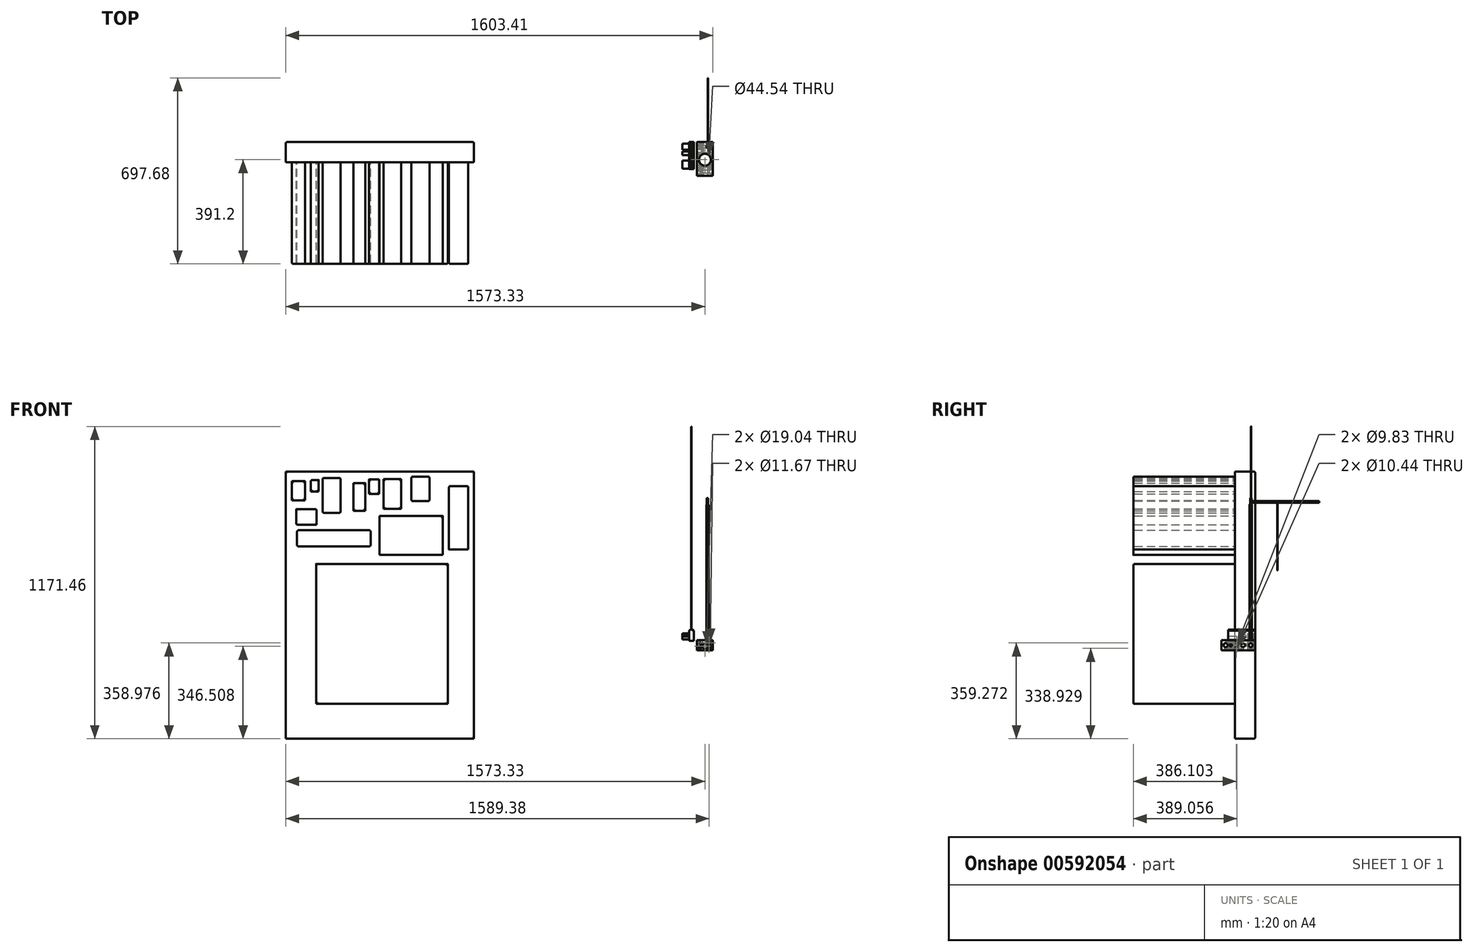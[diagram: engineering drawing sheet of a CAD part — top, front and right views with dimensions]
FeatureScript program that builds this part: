
annotation { "Feature Type Name" : "Feature", "Feature Type Description" : "" }
export const myFeature = defineFeature(function(context is Context, id is Id, definition is map)
    precondition{}
    {
        {
            var Q0;
            Q0=qCreatedBy(makeId("Front.planeOp"),FACE);
            var sketch = newSketch(context, id + "F0", { "sketchPlane" : qUnion([Q0])});
            skLineSegment(sketch, "E0.bottom", {"start": v(30.08, 19.43) * mm, "end": v(-30.08, 19.43) * mm});
            skLineSegment(sketch, "E0.top", {"start": v(30.08, -19.43) * mm, "end": v(-30.08, -19.43) * mm});
            skLineSegment(sketch, "E0.left", {"start": v(30.08, 19.43) * mm, "end": v(30.08, -19.43) * mm});
            skLineSegment(sketch, "E0.right", {"start": v(-30.08, 19.43) * mm, "end": v(-30.08, -19.43) * mm});
            skPoint(sketch, "E0.middle", {"position": v(0, 0) * mm});
            skSolve(sketch);
        }
        {
            var Q0;
            Q0 = qSketchRegion(id + "F0", true);
            extrude(context, id + "F1", {"entities" : qUnion([Q0]), "depth" : 127 * mm, "offsetDistance" : 25.4 * mm});
        }
        {
            var Q0;
            Q0=makeQuery(id+"F1.opExtrude","SWEPT_FACE",FACE,{"disambiguationData":[OSD([sQuery(id+"F0.wireOp",EDGE,"E0.bottom")])]});
            var sketch = newSketch(context, id + "F2", { "sketchPlane" : qUnion([Q0])});
            skCircle(sketch, "E1", {"center": v(0, -66) * mm, "radius": 22.27 * mm});
            skSolve(sketch);
        }
        {
            var Q0;
            Q0=makeQuery(id+"F2.imprint","IMPRINT",FACE,{"disambiguationData":[TD([[makeQuery(id+"F2.imprint","IMPRINT",EDGE,{"derivedFrom":sQuery(id+"F2.wireOp",EDGE,"E1")}),1.0]])]});
            extrude(context, id + "F3", {"entities" : qUnion([Q0]), "operationType" : NewBodyOperationType.REMOVE, "oppositeDirection" : true, "depth" : 127 * mm, "offsetDistance" : 25.4 * mm});
        }
        {
            var Q0;
            Q0=qCreatedBy(makeId("Front.planeOp"),FACE);
            var sketch = newSketch(context, id + "F4", { "sketchPlane" : qUnion([Q0])});
            skLineSegment(sketch, "E2", {"start": v(-59.14, 54.54) * mm, "end": v(-59.14, 17.12) * mm});
            skLineSegment(sketch, "E3", {"start": v(-41.3, 54.83) * mm, "end": v(-41.3, 17.12) * mm});
            skLineSegment(sketch, "E4", {"start": v(-59.14, 54.54) * mm, "end": v(-55.4, 58.77) * mm});
            skLineSegment(sketch, "E5", {"start": v(-55.4, 58.77) * mm, "end": v(-48.5, 58.77) * mm});
            skLineSegment(sketch, "E6", {"start": v(-48.5, 58.77) * mm, "end": v(-41.3, 54.83) * mm});
            skLineSegment(sketch, "E7", {"start": v(-59.14, 17.12) * mm, "end": v(-41.3, 17.12) * mm});
            skSolve(sketch);
        }
        {
            var Q0;
            Q0=makeQuery(id+"F4.imprint","IMPRINT",FACE,{"disambiguationData":[TD([[makeQuery(id+"F4.imprint","IMPRINT",EDGE,{"derivedFrom":sQuery(id+"F4.wireOp",EDGE,"E2")}),1.0]])]});
            extrude(context, id + "F5", {"entities" : qUnion([Q0]), "depth" : 101.6 * mm, "offsetDistance" : 25.4 * mm});
        }
        {
            var Q0;
            Q0=makeQuery(id+"F1.opExtrude","SWEPT_FACE",FACE,{"disambiguationData":[OSD([sQuery(id+"F0.wireOp",EDGE,"E0.left")])]});
            var sketch = newSketch(context, id + "F6", { "sketchPlane" : qUnion([Q0])});
            skCircle(sketch, "E8", {"center": v(-68.14, 8.58) * mm, "radius": 4.91 * mm});
            skSolve(sketch);
        }
        {
            var Q0;
            Q0 = qSketchRegion(id + "F6", true);
            extrude(context, id + "F7", {"entities" : qUnion([Q0]), "operationType" : NewBodyOperationType.REMOVE, "oppositeDirection" : true, "depth" : 254 * mm, "offsetDistance" : 25.4 * mm});
        }
        {
            var Q0;
            Q0=makeQuery(id+"F1.opExtrude","SWEPT_FACE",FACE,{"disambiguationData":[OSD([sQuery(id+"F0.wireOp",EDGE,"E0.left")])]});
            var sketch = newSketch(context, id + "F8", { "sketchPlane" : qUnion([Q0])});
            skCircle(sketch, "E9", {"center": v(-16.75, 0) * mm, "radius": 7.15 * mm});
            skCircle(sketch, "E10", {"center": v(-45.17, 0) * mm, "radius": 7.1 * mm});
            skCircle(sketch, "E11", {"center": v(-71.1, -11.76) * mm, "radius": 5.22 * mm});
            skCircle(sketch, "E12", {"center": v(-91.47, 0) * mm, "radius": 4.6 * mm});
            skCircle(sketch, "E13", {"center": v(-110.6, 0) * mm, "radius": 7.6 * mm});
            skSolve(sketch);
        }
        {
            var Q0;
            Q0=makeQuery(id+"F8.imprint","IMPRINT",FACE,{"disambiguationData":[TD([[makeQuery(id+"F8.imprint","IMPRINT",EDGE,{"derivedFrom":sQuery(id+"F8.wireOp",EDGE,"E13")}),1.0]])]});
            var Q1;
            Q1=makeQuery(id+"F8.imprint","IMPRINT",FACE,{"disambiguationData":[TD([[makeQuery(id+"F8.imprint","IMPRINT",EDGE,{"derivedFrom":sQuery(id+"F8.wireOp",EDGE,"E12")}),1.0]])]});
            var Q2;
            Q2=makeQuery(id+"F8.imprint","IMPRINT",FACE,{"disambiguationData":[TD([[makeQuery(id+"F8.imprint","IMPRINT",EDGE,{"derivedFrom":sQuery(id+"F8.wireOp",EDGE,"E11")}),1.0]])]});
            var Q3;
            Q3=makeQuery(id+"F8.imprint","IMPRINT",FACE,{"disambiguationData":[TD([[makeQuery(id+"F8.imprint","IMPRINT",EDGE,{"derivedFrom":sQuery(id+"F8.wireOp",EDGE,"E10")}),1.0]])]});
            var Q4;
            Q4=makeQuery(id+"F8.imprint","IMPRINT",FACE,{"disambiguationData":[TD([[makeQuery(id+"F8.imprint","IMPRINT",EDGE,{"derivedFrom":sQuery(id+"F8.wireOp",EDGE,"E9")}),1.0]])]});
            extrude(context, id + "F9", {"entities" : qUnion([Q0, Q1, Q2, Q3, Q4]), "operationType" : NewBodyOperationType.REMOVE, "oppositeDirection" : true, "depth" : 254 * mm, "offsetDistance" : 25.4 * mm});
        }
        {
            var Q0;
            Q0=makeQuery(id+"F1.opExtrude","CAP_FACE",FACE,{"disambiguationData":[OSD([sQuery(id+"F0.wireOp",EDGE,"E0.bottom"),sQuery(id+"F0.wireOp",EDGE,"E0.top"),sQuery(id+"F0.wireOp",EDGE,"E0.left"),sQuery(id+"F0.wireOp",EDGE,"E0.right")])],"isStart":false});
            var sketch = newSketch(context, id + "F10", { "sketchPlane" : qUnion([Q0])});
            skCircle(sketch, "E14", {"center": v(-17.6, -8.4) * mm, "radius": 4.93 * mm});
            skCircle(sketch, "E15", {"center": v(-17, 7.55) * mm, "radius": 2.32 * mm});
            skCircle(sketch, "E16", {"center": v(-9.56, 5.12) * mm, "radius": 3.65 * mm});
            skCircle(sketch, "E17", {"center": v(0, -4.18) * mm, "radius": 9.52 * mm});
            skCircle(sketch, "E18", {"center": v(16.04, 8.29) * mm, "radius": 5.84 * mm});
            skCircle(sketch, "E19", {"center": v(21.54, -7.8) * mm, "radius": 4.4 * mm});
            skCircle(sketch, "E20", {"center": v(13.11, -13.57) * mm, "radius": 4.08 * mm});
            skSolve(sketch);
        }
        {
            var Q0;
            Q0 = qSketchRegion(id + "F10", true);
            extrude(context, id + "F11", {"entities" : qUnion([Q0]), "operationType" : NewBodyOperationType.REMOVE, "oppositeDirection" : true, "depth" : 254 * mm, "offsetDistance" : 25.4 * mm});
        }
        {
            var Q0;
            Q0=makeQuery(id+"F5.opExtrude","SWEPT_FACE",FACE,{"disambiguationData":[OSD([sQuery(id+"F4.wireOp",EDGE,"E2")])]});
            var sketch = newSketch(context, id + "F12", { "sketchPlane" : qUnion([Q0])});
            skLineSegment(sketch, "E21.bottom", {"start": v(69.72, 33) * mm, "end": v(99.84, 33) * mm});
            skLineSegment(sketch, "E21.top", {"start": v(69.72, 21.6) * mm, "end": v(99.84, 21.6) * mm});
            skLineSegment(sketch, "E21.left", {"start": v(69.72, 33) * mm, "end": v(69.72, 21.6) * mm});
            skLineSegment(sketch, "E21.right", {"start": v(99.84, 33) * mm, "end": v(99.84, 21.6) * mm});
            skPoint(sketch, "E21.middle", {"position": v(84.78, 27.3) * mm});
            skLineSegment(sketch, "E22.bottom", {"start": v(34.78, 37.75) * mm, "end": v(48.36, 37.75) * mm});
            skLineSegment(sketch, "E22.top", {"start": v(34.78, 31.82) * mm, "end": v(48.36, 31.82) * mm});
            skLineSegment(sketch, "E22.left", {"start": v(34.78, 37.75) * mm, "end": v(34.78, 31.82) * mm});
            skLineSegment(sketch, "E22.right", {"start": v(48.36, 37.75) * mm, "end": v(48.36, 31.82) * mm});
            skPoint(sketch, "E22.middle", {"position": v(41.57, 34.78) * mm});
            skLineSegment(sketch, "E23.bottom", {"start": v(28.18, 25.53) * mm, "end": v(5.18, 25.53) * mm});
            skLineSegment(sketch, "E23.top", {"start": v(28.18, 44.88) * mm, "end": v(5.18, 44.88) * mm});
            skLineSegment(sketch, "E23.left", {"start": v(28.18, 25.53) * mm, "end": v(28.18, 44.88) * mm});
            skLineSegment(sketch, "E23.right", {"start": v(5.18, 25.53) * mm, "end": v(5.18, 44.88) * mm});
            skPoint(sketch, "E23.middle", {"position": v(16.68, 35.2) * mm});
            skSolve(sketch);
        }
        {
            var Q0;
            Q0 = qSketchRegion(id + "F12", true);
            extrude(context, id + "F13", {"entities" : qUnion([Q0]), "operationType" : NewBodyOperationType.ADD, "depth" : 25.4 * mm, "offsetDistance" : 25.4 * mm});
        }
        {
            var Q0;
            Q0=makeQuery(id+"F1.opExtrude","SWEPT_FACE",FACE,{"disambiguationData":[OSD([sQuery(id+"F0.wireOp",EDGE,"E0.bottom")])]});
            var sketch = newSketch(context, id + "F14", { "sketchPlane" : qUnion([Q0])});
            skCircle(sketch, "E24", {"center": v(9.27, -17.23) * mm, "radius": 4.37 * mm});
            skSolve(sketch);
        }
        {
            var Q0;
            Q0 = qSketchRegion(id + "F14", true);
            extrude(context, id + "F15", {"entities" : qUnion([Q0]), "operationType" : NewBodyOperationType.ADD, "depth" : 508 * mm, "offsetDistance" : 25.4 * mm});
        }
        {
            var Q0;
            Q0=makeQuery(id+"F5.opExtrude","SWEPT_FACE",FACE,{"disambiguationData":[OSD([sQuery(id+"F4.wireOp",EDGE,"E5")])]});
            var sketch = newSketch(context, id + "F16", { "sketchPlane" : qUnion([Q0])});
            skCircle(sketch, "E25", {"center": v(-51.42, -15.39) * mm, "radius": 0.57 * mm});
            skSolve(sketch);
        }
        {
            var Q0;
            Q0 = qSketchRegion(id + "F16", true);
            extrude(context, id + "F17", {"entities" : qUnion([Q0]), "operationType" : NewBodyOperationType.ADD, "depth" : 762 * mm, "offsetDistance" : 25.4 * mm});
        }
        {
            var Q0;
            Q0=makeQuery(id+"F15.opExtrude","CAP_FACE",FACE,{"disambiguationData":[OSD([sQuery(id+"F14.wireOp",EDGE,"E24")])],"isStart":false});
            var sketch = newSketch(context, id + "F18", { "sketchPlane" : qUnion([Q0])});
            skLineSegment(sketch, "E26.bottom", {"start": v(9.3, -16.3) * mm, "end": v(11.43, -16.3) * mm});
            skLineSegment(sketch, "E26.top", {"start": v(9.3, -13.52) * mm, "end": v(11.43, -13.52) * mm});
            skLineSegment(sketch, "E26.left", {"start": v(9.3, -16.3) * mm, "end": v(9.3, -13.52) * mm});
            skLineSegment(sketch, "E26.right", {"start": v(11.43, -16.3) * mm, "end": v(11.43, -13.52) * mm});
            skPoint(sketch, "E26.middle", {"position": v(10.37, -14.9) * mm});
            skLineSegment(sketch, "E27.bottom", {"start": v(8.92, -18.51) * mm, "end": v(9.91, -18.51) * mm});
            skLineSegment(sketch, "E27.top", {"start": v(8.92, -16.37) * mm, "end": v(9.91, -16.37) * mm});
            skLineSegment(sketch, "E27.left", {"start": v(8.92, -18.51) * mm, "end": v(8.92, -16.37) * mm});
            skLineSegment(sketch, "E27.right", {"start": v(9.91, -18.51) * mm, "end": v(9.91, -16.37) * mm});
            skPoint(sketch, "E27.middle", {"position": v(9.42, -17.44) * mm});
            skLineSegment(sketch, "E28.bottom", {"start": v(6.4, -17.92) * mm, "end": v(8.35, -17.92) * mm});
            skLineSegment(sketch, "E28.top", {"start": v(6.4, -14.7) * mm, "end": v(8.35, -14.7) * mm});
            skLineSegment(sketch, "E28.left", {"start": v(6.4, -17.92) * mm, "end": v(6.4, -14.7) * mm});
            skLineSegment(sketch, "E28.right", {"start": v(8.35, -17.92) * mm, "end": v(8.35, -14.7) * mm});
            skPoint(sketch, "E28.middle", {"position": v(7.37, -16.31) * mm});
            skSolve(sketch);
        }
        {
            var Q0;
            Q0 = qSketchRegion(id + "F18", true);
            extrude(context, id + "F19", {"entities" : qUnion([Q0]), "operationType" : NewBodyOperationType.ADD, "depth" : 25.4 * mm, "offsetDistance" : 25.4 * mm});
        }
        {
            var Q0;
            Q0=makeQuery(id+"F19.opExtrude","SWEPT_FACE",FACE,{"disambiguationData":[OSD([sQuery(id+"F18.wireOp",EDGE,"E26.top")])]});
            var sketch = newSketch(context, id + "F20", { "sketchPlane" : qUnion([Q0])});
            skLineSegment(sketch, "E29.bottom", {"start": v(-10, 540.96) * mm, "end": v(-11.1, 540.96) * mm});
            skLineSegment(sketch, "E29.top", {"start": v(-10, 534.92) * mm, "end": v(-11.1, 534.92) * mm});
            skLineSegment(sketch, "E29.left", {"start": v(-10, 540.96) * mm, "end": v(-10, 534.92) * mm});
            skLineSegment(sketch, "E29.right", {"start": v(-11.1, 540.96) * mm, "end": v(-11.1, 534.92) * mm});
            skPoint(sketch, "E29.middle", {"position": v(-10.55, 537.94) * mm});
            skSolve(sketch);
        }
        {
            var Q0;
            Q0 = qSketchRegion(id + "F20", true);
            extrude(context, id + "F21", {"entities" : qUnion([Q0]), "operationType" : NewBodyOperationType.ADD, "depth" : 254 * mm, "offsetDistance" : 25.4 * mm});
        }
        {
            var Q0;
            Q0=makeQuery(id+"F21.opExtrude","SWEPT_FACE",FACE,{"disambiguationData":[OSD([sQuery(id+"F20.wireOp",EDGE,"E29.top")])]});
            var sketch = newSketch(context, id + "F22", { "sketchPlane" : qUnion([Q0])});
            skCircle(sketch, "E30", {"center": v(10.57, -83.53) * mm, "radius": 0.18 * mm});
            skSolve(sketch);
        }
        {
            var Q0;
            Q0 = qSketchRegion(id + "F22", true);
            extrude(context, id + "F23", {"entities" : qUnion([Q0]), "operationType" : NewBodyOperationType.ADD, "depth" : 254 * mm, "offsetDistance" : 25.4 * mm});
        }
        {
            var Q0;
            Q0=qCreatedBy(makeId("Front.planeOp"),FACE);
            var sketch = newSketch(context, id + "F24", { "sketchPlane" : qUnion([Q0])});
            skLineSegment(sketch, "E31.bottom", {"start": v(-866.82, -350.69) * mm, "end": v(-1573.33, -350.69) * mm});
            skLineSegment(sketch, "E31.top", {"start": v(-866.82, 652.1) * mm, "end": v(-1573.33, 652.1) * mm});
            skLineSegment(sketch, "E31.left", {"start": v(-866.82, -350.69) * mm, "end": v(-866.82, 652.1) * mm});
            skLineSegment(sketch, "E31.right", {"start": v(-1573.33, -350.69) * mm, "end": v(-1573.33, 652.1) * mm});
            skPoint(sketch, "E31.middle", {"position": v(-1220.07, 150.7) * mm});
            skSolve(sketch);
        }
        {
            var Q0;
            Q0 = qSketchRegion(id + "F24", true);
            extrude(context, id + "F25", {"entities" : qUnion([Q0]), "depth" : 76.2 * mm, "offsetDistance" : 25.4 * mm});
        }
        {
            var Q0;
            Q0=makeQuery(id+"F25.opExtrude","CAP_FACE",FACE,{"disambiguationData":[OSD([sQuery(id+"F24.wireOp",EDGE,"E31.bottom"),sQuery(id+"F24.wireOp",EDGE,"E31.top"),sQuery(id+"F24.wireOp",EDGE,"E31.left"),sQuery(id+"F24.wireOp",EDGE,"E31.right")])],"isStart":false});
            var sketch = newSketch(context, id + "F26", { "sketchPlane" : qUnion([Q0])});
            skLineSegment(sketch, "E32.bottom", {"start": v(-1501.2, 544.2) * mm, "end": v(-1550.28, 544.2) * mm});
            skLineSegment(sketch, "E32.top", {"start": v(-1501.2, 615.35) * mm, "end": v(-1550.28, 615.35) * mm});
            skLineSegment(sketch, "E32.left", {"start": v(-1501.2, 544.2) * mm, "end": v(-1501.2, 615.35) * mm});
            skLineSegment(sketch, "E32.right", {"start": v(-1550.28, 544.2) * mm, "end": v(-1550.28, 615.35) * mm});
            skPoint(sketch, "E32.middle", {"position": v(-1525.74, 579.77) * mm});
            skLineSegment(sketch, "E33.bottom", {"start": v(-1449.84, 576.02) * mm, "end": v(-1479.44, 576.02) * mm});
            skLineSegment(sketch, "E33.top", {"start": v(-1449.84, 619.96) * mm, "end": v(-1479.44, 619.96) * mm});
            skLineSegment(sketch, "E33.left", {"start": v(-1449.84, 576.02) * mm, "end": v(-1449.84, 619.96) * mm});
            skLineSegment(sketch, "E33.right", {"start": v(-1479.44, 576.02) * mm, "end": v(-1479.44, 619.96) * mm});
            skPoint(sketch, "E33.middle", {"position": v(-1464.64, 598) * mm});
            skLineSegment(sketch, "E34.bottom", {"start": v(-1457.86, 452.43) * mm, "end": v(-1533.97, 452.43) * mm});
            skLineSegment(sketch, "E34.top", {"start": v(-1457.86, 510.53) * mm, "end": v(-1533.97, 510.53) * mm});
            skLineSegment(sketch, "E34.left", {"start": v(-1457.86, 452.43) * mm, "end": v(-1457.86, 510.53) * mm});
            skLineSegment(sketch, "E34.right", {"start": v(-1533.97, 452.43) * mm, "end": v(-1533.97, 510.53) * mm});
            skPoint(sketch, "E34.middle", {"position": v(-1495.92, 481.48) * mm});
            skLineSegment(sketch, "E35.bottom", {"start": v(-1367.21, 497.11) * mm, "end": v(-1435.46, 497.11) * mm});
            skLineSegment(sketch, "E35.top", {"start": v(-1367.21, 627.57) * mm, "end": v(-1435.46, 627.57) * mm});
            skLineSegment(sketch, "E35.left", {"start": v(-1367.21, 497.11) * mm, "end": v(-1367.21, 627.57) * mm});
            skLineSegment(sketch, "E35.right", {"start": v(-1435.46, 497.11) * mm, "end": v(-1435.46, 627.57) * mm});
            skPoint(sketch, "E35.middle", {"position": v(-1401.34, 562.34) * mm});
            skLineSegment(sketch, "E36.bottom", {"start": v(-1274.2, 503.97) * mm, "end": v(-1318.99, 503.97) * mm});
            skLineSegment(sketch, "E36.top", {"start": v(-1274.2, 608.19) * mm, "end": v(-1318.99, 608.19) * mm});
            skLineSegment(sketch, "E36.left", {"start": v(-1274.2, 503.97) * mm, "end": v(-1274.2, 608.19) * mm});
            skLineSegment(sketch, "E36.right", {"start": v(-1318.99, 503.97) * mm, "end": v(-1318.99, 608.19) * mm});
            skPoint(sketch, "E36.middle", {"position": v(-1296.6, 556.08) * mm});
            skLineSegment(sketch, "E37.bottom", {"start": v(-1254.63, 371.16) * mm, "end": v(-1530.85, 371.16) * mm});
            skLineSegment(sketch, "E37.top", {"start": v(-1254.63, 431.29) * mm, "end": v(-1530.85, 431.29) * mm});
            skLineSegment(sketch, "E37.left", {"start": v(-1254.63, 371.16) * mm, "end": v(-1254.63, 431.29) * mm});
            skLineSegment(sketch, "E37.right", {"start": v(-1530.85, 371.16) * mm, "end": v(-1530.85, 431.29) * mm});
            skPoint(sketch, "E37.middle", {"position": v(-1392.74, 401.22) * mm});
            skLineSegment(sketch, "E38.bottom", {"start": v(-1222.51, 567.89) * mm, "end": v(-1261.5, 567.89) * mm});
            skLineSegment(sketch, "E38.top", {"start": v(-1222.51, 622.32) * mm, "end": v(-1261.5, 622.32) * mm});
            skLineSegment(sketch, "E38.left", {"start": v(-1222.51, 567.89) * mm, "end": v(-1222.51, 622.32) * mm});
            skLineSegment(sketch, "E38.right", {"start": v(-1261.5, 567.89) * mm, "end": v(-1261.5, 622.32) * mm});
            skPoint(sketch, "E38.middle", {"position": v(-1242, 595.1) * mm});
            skLineSegment(sketch, "E39.bottom", {"start": v(-965.38, -220.28) * mm, "end": v(-1459, -220.28) * mm});
            skLineSegment(sketch, "E39.top", {"start": v(-965.38, 304.92) * mm, "end": v(-1459, 304.92) * mm});
            skLineSegment(sketch, "E39.left", {"start": v(-965.38, -220.28) * mm, "end": v(-965.38, 304.92) * mm});
            skLineSegment(sketch, "E39.right", {"start": v(-1459, -220.28) * mm, "end": v(-1459, 304.92) * mm});
            skPoint(sketch, "E39.middle", {"position": v(-1212.2, 42.32) * mm});
            skLineSegment(sketch, "E40.bottom", {"start": v(-1140.45, 511.24) * mm, "end": v(-1206.51, 511.24) * mm});
            skLineSegment(sketch, "E40.top", {"start": v(-1140.45, 623.03) * mm, "end": v(-1206.51, 623.03) * mm});
            skLineSegment(sketch, "E40.left", {"start": v(-1140.45, 511.24) * mm, "end": v(-1140.45, 623.03) * mm});
            skLineSegment(sketch, "E40.right", {"start": v(-1206.51, 511.24) * mm, "end": v(-1206.51, 623.03) * mm});
            skPoint(sketch, "E40.middle", {"position": v(-1173.48, 567.14) * mm});
            skLineSegment(sketch, "E41.bottom", {"start": v(-1033.75, 540.67) * mm, "end": v(-1101.6, 540.67) * mm});
            skLineSegment(sketch, "E41.top", {"start": v(-1033.75, 632.82) * mm, "end": v(-1101.6, 632.82) * mm});
            skLineSegment(sketch, "E41.left", {"start": v(-1033.75, 540.67) * mm, "end": v(-1033.75, 632.82) * mm});
            skLineSegment(sketch, "E41.right", {"start": v(-1101.6, 540.67) * mm, "end": v(-1101.6, 632.82) * mm});
            skPoint(sketch, "E41.middle", {"position": v(-1067.67, 586.74) * mm});
            skLineSegment(sketch, "E42.bottom", {"start": v(-983.66, 338.54) * mm, "end": v(-1221, 338.54) * mm});
            skLineSegment(sketch, "E42.top", {"start": v(-983.66, 485.04) * mm, "end": v(-1221, 485.04) * mm});
            skLineSegment(sketch, "E42.left", {"start": v(-983.66, 338.54) * mm, "end": v(-983.66, 485.04) * mm});
            skLineSegment(sketch, "E42.right", {"start": v(-1221, 338.54) * mm, "end": v(-1221, 485.04) * mm});
            skPoint(sketch, "E42.middle", {"position": v(-1102.33, 411.8) * mm});
            skLineSegment(sketch, "E43.bottom", {"start": v(-888.13, 358.82) * mm, "end": v(-960.78, 358.82) * mm});
            skLineSegment(sketch, "E43.top", {"start": v(-888.13, 597.01) * mm, "end": v(-960.78, 597.01) * mm});
            skLineSegment(sketch, "E43.left", {"start": v(-888.13, 358.82) * mm, "end": v(-888.13, 597.01) * mm});
            skLineSegment(sketch, "E43.right", {"start": v(-960.78, 358.82) * mm, "end": v(-960.78, 597.01) * mm});
            skPoint(sketch, "E43.middle", {"position": v(-924.46, 477.92) * mm});
            skSolve(sketch);
        }
        {
            var Q0;
            Q0 = qSketchRegion(id + "F26", true);
            extrude(context, id + "F27", {"entities" : qUnion([Q0]), "operationType" : NewBodyOperationType.ADD, "depth" : 381 * mm, "offsetDistance" : 25.4 * mm});
        }
        {
            var Q0;
            Q0=makeQuery(id+"F27.opExtrude","SWEPT_EDGE",EDGE,{"disambiguationData":[OSD([sQuery(id+"F26.wireOp",EDGE,"E43.top"),sQuery(id+"F26.wireOp",EDGE,"E43.left")])]});
            fillet(context, id + "F28", {"entities" : qUnion([Q0]), "radius" : 5.08 * mm, "tangentPropagation" : true, "allowEdgeOverflow" : false});
        }
        {
            var Q0;
            Q0=makeQuery(id+"F27.opExtrude","SWEPT_EDGE",EDGE,{"disambiguationData":[OSD([sQuery(id+"F26.wireOp",EDGE,"E43.top"),sQuery(id+"F26.wireOp",EDGE,"E43.right")])]});
            var Q1;
            Q1=makeQuery(id+"F27.opExtrude","CAP_EDGE",EDGE,{"disambiguationData":[OSD([sQuery(id+"F26.wireOp",EDGE,"E43.right")])],"isStart":false});
            var Q2;
            Q2=makeQuery(id+"F27.opExtrude","CAP_EDGE",EDGE,{"disambiguationData":[OSD([sQuery(id+"F26.wireOp",EDGE,"E43.right")])],"isStart":true});
            var Q3;
            Q3=makeQuery(id+"F27.opExtrude","CAP_EDGE",EDGE,{"disambiguationData":[OSD([sQuery(id+"F26.wireOp",EDGE,"E42.top")])],"isStart":false});
            var Q4;
            Q4=makeQuery(id+"F27.opExtrude","CAP_EDGE",EDGE,{"disambiguationData":[OSD([sQuery(id+"F26.wireOp",EDGE,"E42.left")])],"isStart":false});
            var Q5;
            Q5=makeQuery(id+"F27.opExtrude","CAP_EDGE",EDGE,{"disambiguationData":[OSD([sQuery(id+"F26.wireOp",EDGE,"E41.bottom")])],"isStart":false});
            var Q6;
            Q6=makeQuery(id+"F27.opExtrude","CAP_EDGE",EDGE,{"disambiguationData":[OSD([sQuery(id+"F26.wireOp",EDGE,"E41.left")])],"isStart":false});
            var Q7;
            Q7=makeQuery(id+"F27.opExtrude","SWEPT_EDGE",EDGE,{"disambiguationData":[OSD([sQuery(id+"F26.wireOp",EDGE,"E41.bottom"),sQuery(id+"F26.wireOp",EDGE,"E41.left")])]});
            fillet(context, id + "F29", {"entities" : qUnion([Q0, Q1, Q2, Q3, Q4, Q5, Q6, Q7]), "radius" : 5.08 * mm, "tangentPropagation" : true, "allowEdgeOverflow" : false});
        }
        {
            var Q0;
            Q0=makeQuery(id+"F27.opExtrude","CAP_EDGE",EDGE,{"disambiguationData":[OSD([sQuery(id+"F26.wireOp",EDGE,"E43.top")])],"isStart":false});
            fillet(context, id + "F30", {"entities" : qUnion([Q0]), "radius" : 5.08 * mm, "tangentPropagation" : true, "allowEdgeOverflow" : false});
        }
        {
            var Q0;
            Q0=makeQuery(id+"F27.opExtrude","CAP_EDGE",EDGE,{"disambiguationData":[OSD([sQuery(id+"F26.wireOp",EDGE,"E41.right")])],"isStart":false});
            var Q1;
            Q1=makeQuery(id+"F27.opExtrude","SWEPT_EDGE",EDGE,{"disambiguationData":[OSD([sQuery(id+"F26.wireOp",EDGE,"E41.top"),sQuery(id+"F26.wireOp",EDGE,"E41.right")])]});
            var Q2;
            Q2=makeQuery(id+"F27.opExtrude","CAP_EDGE",EDGE,{"disambiguationData":[OSD([sQuery(id+"F26.wireOp",EDGE,"E41.top")])],"isStart":false});
            var Q3;
            Q3=makeQuery(id+"F27.opExtrude","SWEPT_EDGE",EDGE,{"disambiguationData":[OSD([sQuery(id+"F26.wireOp",EDGE,"E41.top"),sQuery(id+"F26.wireOp",EDGE,"E41.left")])]});
            fillet(context, id + "F31", {"entities" : qUnion([Q0, Q1, Q2, Q3]), "radius" : 5.08 * mm, "tangentPropagation" : true, "allowEdgeOverflow" : false});
        }
        {
            var Q0;
            Q0=makeQuery(id+"F27.opExtrude","CAP_EDGE",EDGE,{"disambiguationData":[OSD([sQuery(id+"F26.wireOp",EDGE,"E39.top")])],"isStart":false});
            var Q1;
            Q1=makeQuery(id+"F27.opExtrude","CAP_EDGE",EDGE,{"disambiguationData":[OSD([sQuery(id+"F26.wireOp",EDGE,"E39.left")])],"isStart":false});
            var Q2;
            Q2=makeQuery(id+"F27.opExtrude","CAP_EDGE",EDGE,{"disambiguationData":[OSD([sQuery(id+"F26.wireOp",EDGE,"E39.bottom")])],"isStart":false});
            var Q3;
            Q3=makeQuery(id+"F27.opExtrude","CAP_EDGE",EDGE,{"disambiguationData":[OSD([sQuery(id+"F26.wireOp",EDGE,"E39.right")])],"isStart":false});
            var Q4;
            Q4=makeQuery(id+"F27.opExtrude","CAP_EDGE",EDGE,{"disambiguationData":[OSD([sQuery(id+"F26.wireOp",EDGE,"E37.bottom")])],"isStart":false});
            var Q5;
            Q5=makeQuery(id+"F27.opExtrude","CAP_EDGE",EDGE,{"disambiguationData":[OSD([sQuery(id+"F26.wireOp",EDGE,"E37.top")])],"isStart":false});
            var Q6;
            Q6=makeQuery(id+"F27.opExtrude","CAP_EDGE",EDGE,{"disambiguationData":[OSD([sQuery(id+"F26.wireOp",EDGE,"E35.left")])],"isStart":false});
            var Q7;
            Q7=makeQuery(id+"F27.opExtrude","CAP_EDGE",EDGE,{"disambiguationData":[OSD([sQuery(id+"F26.wireOp",EDGE,"E35.right")])],"isStart":false});
            fillet(context, id + "F32", {"entities" : qUnion([Q0, Q1, Q2, Q3, Q4, Q5, Q6, Q7]), "radius" : 5.08 * mm, "tangentPropagation" : true, "allowEdgeOverflow" : false});
        }
        {
            var Q0;
            Q0=makeQuery(id+"F27.opExtrude","CAP_EDGE",EDGE,{"disambiguationData":[OSD([sQuery(id+"F26.wireOp",EDGE,"E37.left")])],"isStart":false});
            var Q1;
            Q1=makeQuery(id+"F27.opExtrude","CAP_EDGE",EDGE,{"disambiguationData":[OSD([sQuery(id+"F26.wireOp",EDGE,"E34.left")])],"isStart":false});
            var Q2;
            Q2=makeQuery(id+"F27.opExtrude","CAP_EDGE",EDGE,{"disambiguationData":[OSD([sQuery(id+"F26.wireOp",EDGE,"E34.bottom")])],"isStart":false});
            fillet(context, id + "F33", {"entities" : qUnion([Q0, Q1, Q2]), "radius" : 5.08 * mm, "tangentPropagation" : true, "allowEdgeOverflow" : false});
        }
        {
            var Q0;
            Q0=makeQuery(id+"F27.opExtrude","CAP_EDGE",EDGE,{"disambiguationData":[OSD([sQuery(id+"F26.wireOp",EDGE,"E37.right")])],"isStart":false});
            var Q1;
            Q1=makeQuery(id+"F27.opExtrude","CAP_EDGE",EDGE,{"disambiguationData":[OSD([sQuery(id+"F26.wireOp",EDGE,"E34.right")])],"isStart":false});
            var Q2;
            Q2=makeQuery(id+"F27.opExtrude","CAP_EDGE",EDGE,{"disambiguationData":[OSD([sQuery(id+"F26.wireOp",EDGE,"E34.top")])],"isStart":false});
            var Q3;
            Q3=makeQuery(id+"F27.opExtrude","CAP_EDGE",EDGE,{"disambiguationData":[OSD([sQuery(id+"F26.wireOp",EDGE,"E32.bottom")])],"isStart":false});
            var Q4;
            Q4=makeQuery(id+"F27.opExtrude","CAP_EDGE",EDGE,{"disambiguationData":[OSD([sQuery(id+"F26.wireOp",EDGE,"E32.left")])],"isStart":false});
            var Q5;
            Q5=makeQuery(id+"F27.opExtrude","CAP_EDGE",EDGE,{"disambiguationData":[OSD([sQuery(id+"F26.wireOp",EDGE,"E32.right")])],"isStart":false});
            var Q6;
            Q6=makeQuery(id+"F27.opExtrude","CAP_EDGE",EDGE,{"disambiguationData":[OSD([sQuery(id+"F26.wireOp",EDGE,"E35.bottom")])],"isStart":false});
            var Q7;
            Q7=makeQuery(id+"F27.opExtrude","CAP_EDGE",EDGE,{"disambiguationData":[OSD([sQuery(id+"F26.wireOp",EDGE,"E33.bottom")])],"isStart":false});
            var Q8;
            Q8=makeQuery(id+"F27.opExtrude","CAP_EDGE",EDGE,{"disambiguationData":[OSD([sQuery(id+"F26.wireOp",EDGE,"E33.left")])],"isStart":false});
            var Q9;
            Q9=makeQuery(id+"F27.opExtrude","CAP_EDGE",EDGE,{"disambiguationData":[OSD([sQuery(id+"F26.wireOp",EDGE,"E33.right")])],"isStart":false});
            var Q10;
            Q10=makeQuery(id+"F27.opExtrude","CAP_EDGE",EDGE,{"disambiguationData":[OSD([sQuery(id+"F26.wireOp",EDGE,"E33.top")])],"isStart":false});
            var Q11;
            Q11=makeQuery(id+"F27.opExtrude","CAP_EDGE",EDGE,{"disambiguationData":[OSD([sQuery(id+"F26.wireOp",EDGE,"E32.top")])],"isStart":false});
            var Q12;
            Q12=makeQuery(id+"F27.opExtrude","CAP_EDGE",EDGE,{"disambiguationData":[OSD([sQuery(id+"F26.wireOp",EDGE,"E35.top")])],"isStart":false});
            var Q13;
            Q13=makeQuery(id+"F27.opExtrude","CAP_EDGE",EDGE,{"disambiguationData":[OSD([sQuery(id+"F26.wireOp",EDGE,"E36.top")])],"isStart":false});
            var Q14;
            Q14=makeQuery(id+"F27.opExtrude","CAP_EDGE",EDGE,{"disambiguationData":[OSD([sQuery(id+"F26.wireOp",EDGE,"E36.right")])],"isStart":false});
            var Q15;
            Q15=makeQuery(id+"F27.opExtrude","CAP_EDGE",EDGE,{"disambiguationData":[OSD([sQuery(id+"F26.wireOp",EDGE,"E36.left")])],"isStart":false});
            var Q16;
            Q16=makeQuery(id+"F27.opExtrude","CAP_EDGE",EDGE,{"disambiguationData":[OSD([sQuery(id+"F26.wireOp",EDGE,"E36.bottom")])],"isStart":false});
            var Q17;
            Q17=makeQuery(id+"F27.opExtrude","CAP_EDGE",EDGE,{"disambiguationData":[OSD([sQuery(id+"F26.wireOp",EDGE,"E38.bottom")])],"isStart":false});
            var Q18;
            Q18=makeQuery(id+"F27.opExtrude","CAP_EDGE",EDGE,{"disambiguationData":[OSD([sQuery(id+"F26.wireOp",EDGE,"E38.left")])],"isStart":false});
            var Q19;
            Q19=makeQuery(id+"F25.opExtrude","CAP_FACE",FACE,{"disambiguationData":[OSD([sQuery(id+"F24.wireOp",EDGE,"E31.bottom"),sQuery(id+"F24.wireOp",EDGE,"E31.top"),sQuery(id+"F24.wireOp",EDGE,"E31.left"),sQuery(id+"F24.wireOp",EDGE,"E31.right")])],"isStart":true});
            var Q20;
            Q20=makeQuery(id+"F27.opExtrude","CAP_EDGE",EDGE,{"disambiguationData":[OSD([sQuery(id+"F26.wireOp",EDGE,"E38.right")])],"isStart":false});
            var Q21;
            Q21=makeQuery(id+"F27.opExtrude","CAP_EDGE",EDGE,{"disambiguationData":[OSD([sQuery(id+"F26.wireOp",EDGE,"E38.top")])],"isStart":false});
            var Q22;
            Q22=makeQuery(id+"F27.opExtrude","CAP_EDGE",EDGE,{"disambiguationData":[OSD([sQuery(id+"F26.wireOp",EDGE,"E40.top")])],"isStart":false});
            var Q23;
            Q23=makeQuery(id+"F27.opExtrude","CAP_EDGE",EDGE,{"disambiguationData":[OSD([sQuery(id+"F26.wireOp",EDGE,"E40.right")])],"isStart":false});
            var Q24;
            Q24=makeQuery(id+"F27.opExtrude","CAP_EDGE",EDGE,{"disambiguationData":[OSD([sQuery(id+"F26.wireOp",EDGE,"E40.left")])],"isStart":false});
            var Q25;
            Q25=makeQuery(id+"F27.opExtrude","CAP_EDGE",EDGE,{"disambiguationData":[OSD([sQuery(id+"F26.wireOp",EDGE,"E40.bottom")])],"isStart":false});
            fillet(context, id + "F34", {"entities" : qUnion([Q0, Q1, Q2, Q3, Q4, Q5, Q6, Q7, Q8, Q9, Q10, Q11, Q12, Q13, Q14, Q15, Q16, Q17, Q18, Q19, Q20, Q21, Q22, Q23, Q24, Q25]), "radius" : 5.08 * mm, "tangentPropagation" : true, "allowEdgeOverflow" : false});
        }
        {
            var Q0;
            Q0=makeQuery(id+"F27.opExtrude","SWEPT_EDGE",EDGE,{"disambiguationData":[OSD([sQuery(id+"F26.wireOp",EDGE,"E33.top"),sQuery(id+"F26.wireOp",EDGE,"E33.right")])]});
            fillet(context, id + "F35", {"entities" : qUnion([Q0]), "radius" : 5.08 * mm, "tangentPropagation" : true, "allowEdgeOverflow" : false});
        }
    });
